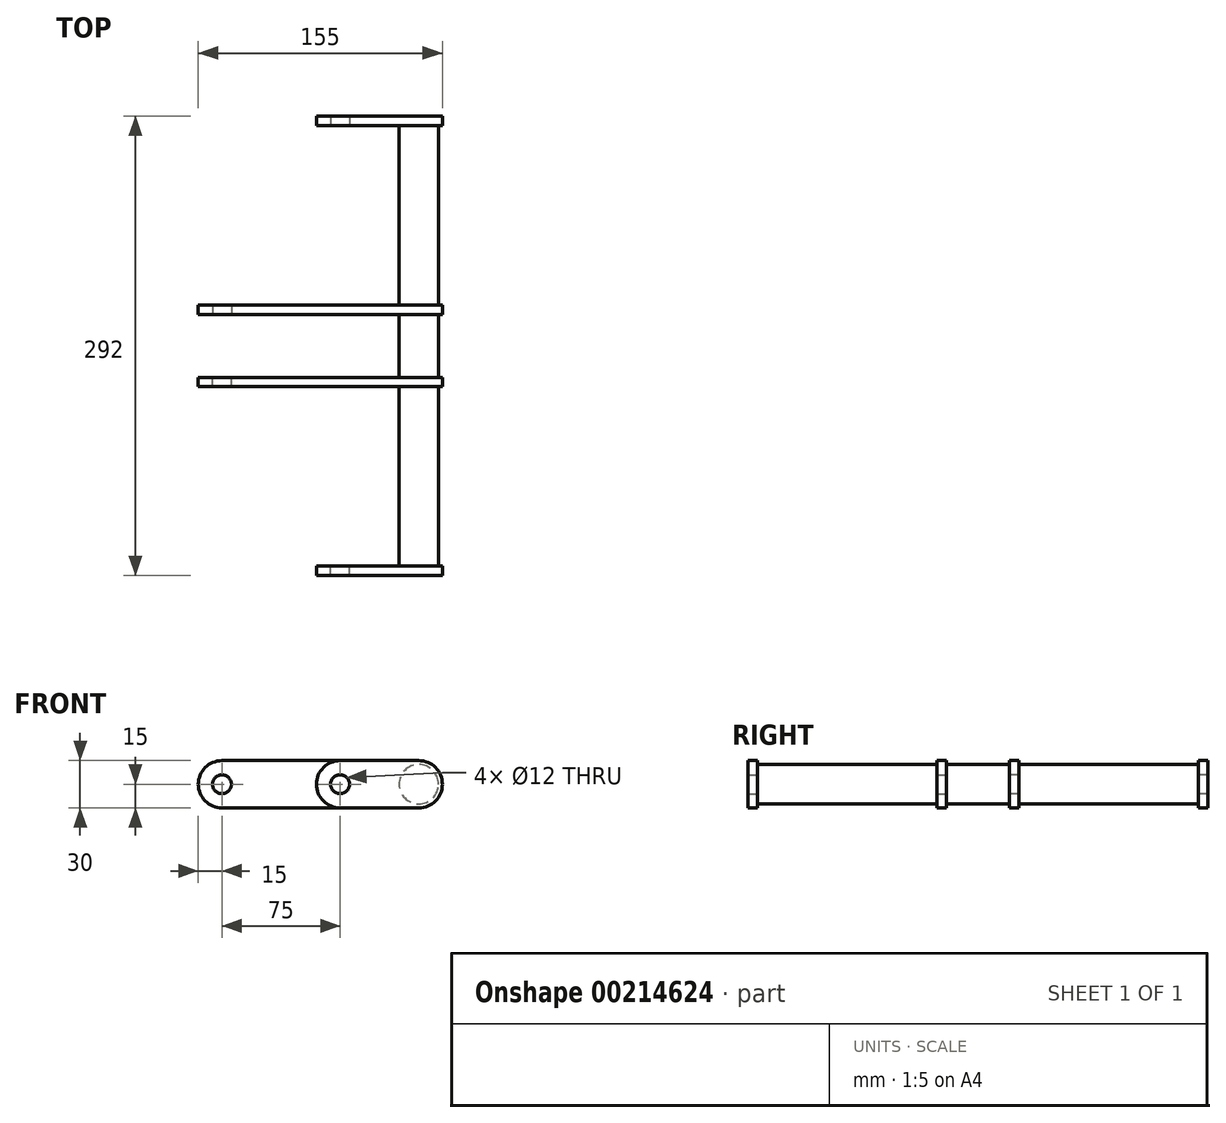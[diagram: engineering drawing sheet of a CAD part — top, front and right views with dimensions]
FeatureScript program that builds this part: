
annotation { "Feature Type Name" : "Feature", "Feature Type Description" : "" }
export const myFeature = defineFeature(function(context is Context, id is Id, definition is map)
    precondition{}
    {
        {
            var Q0;
            Q0=qCreatedBy(makeId("Front.planeOp"),FACE);
            cPlane(context, id + "F0", {"entities" : qUnion([Q0]), "cplaneType" : CPlaneType.OFFSET, "offset" : 140 * mm, "width" : 150 * mm, "height" : 150 * mm});
        }
        {
            var Q0;
            Q0=qCreatedBy(id+"F0.planeOp",FACE);
            var sketch = newSketch(context, id + "F1", { "sketchPlane" : qUnion([Q0])});
            skPoint(sketch, "E0.0", {"position": v(0, 0) * mm});
            skArc(sketch, "E1", {"start": v(0, -15) * mm, "mid": v(15, 0) * mm, "end": v(0, 15) * mm});
            skArc(sketch, "E2", {"start": v(-50, 15) * mm, "mid": v(-65, 0) * mm, "end": v(-50, -15) * mm});
            skCircle(sketch, "E3", {"center": v(0, 0) * mm, "radius": 6 * mm});
            skCircle(sketch, "E4", {"center": v(-50, 0) * mm, "radius": 6 * mm});
            skCircle(sketch, "E5", {"center": v(0, 0) * mm, "radius": 12.5 * mm});
            skLineSegment(sketch, "E6", {"start": v(0, 0) * mm, "end": v(-50, 0) * mm, "construction": true});
            skLineSegment(sketch, "E7", {"start": v(-50, 15) * mm, "end": v(0, 15) * mm});
            skLineSegment(sketch, "E8", {"start": v(0, -15) * mm, "end": v(-50, -15) * mm});
            skSolve(sketch);
        }
        {
            var Q0;
            Q0=makeQuery(id+"F1.imprint","IMPRINT",FACE,{"disambiguationData":[TD([[makeQuery(id+"F1.imprint","IMPRINT",EDGE,{"derivedFrom":sQuery(id+"F1.wireOp",EDGE,"E1")}),1.0]])]});
            var Q1;
            Q1=makeQuery(id+"F1.imprint","IMPRINT",FACE,{"disambiguationData":[TD([[makeQuery(id+"F1.imprint","IMPRINT",EDGE,{"derivedFrom":sQuery(id+"F1.wireOp",EDGE,"E3")}),-1.0]])]});
            var Q2;
            Q2=makeQuery(id+"F1.imprint","IMPRINT",FACE,{"disambiguationData":[TD([[makeQuery(id+"F1.imprint","IMPRINT",EDGE,{"derivedFrom":sQuery(id+"F1.wireOp",EDGE,"E3")}),1.0]])]});
            extrude(context, id + "F2", {"entities" : qUnion([Q0, Q1, Q2]), "depth" : 6 * mm});
        }
        {
            var Q0;
            Q0=makeQuery(id+"F1.imprint","IMPRINT",FACE,{"disambiguationData":[TD([[makeQuery(id+"F1.imprint","IMPRINT",EDGE,{"derivedFrom":sQuery(id+"F1.wireOp",EDGE,"E3")}),-1.0]])]});
            var Q1;
            Q1=makeQuery(id+"F1.imprint","IMPRINT",FACE,{"disambiguationData":[TD([[makeQuery(id+"F1.imprint","IMPRINT",EDGE,{"derivedFrom":sQuery(id+"F1.wireOp",EDGE,"E3")}),1.0]])]});
            var Q2;
            Q2=qCreatedBy(makeId("Front.planeOp"),FACE);
            extrude(context, id + "F3", {"entities" : qUnion([Q0, Q1]), "operationType" : NewBodyOperationType.ADD, "endBound" : BoundingType.UP_TO_SURFACE, "oppositeDirection" : true, "endBoundEntityFace" : qUnion([Q2]), "depth" : 25 * mm});
        }
        {
            var Q0;
            Q0=qCreatedBy(makeId("Front.planeOp"),FACE);
            cPlane(context, id + "F4", {"entities" : qUnion([Q0]), "cplaneType" : CPlaneType.OFFSET, "offset" : 20 * mm, "width" : 150 * mm, "height" : 150 * mm});
        }
        {
            var Q0;
            Q0=qCreatedBy(id+"F4.planeOp",FACE);
            var sketch = newSketch(context, id + "F5", { "sketchPlane" : qUnion([Q0])});
            skArc(sketch, "E9.0", {"start": v(0, -15) * mm, "mid": v(15, 0) * mm, "end": v(0, 15) * mm});
            skArc(sketch, "E10", {"start": v(-125, 15) * mm, "mid": v(-140, 0) * mm, "end": v(-125, -15) * mm});
            skCircle(sketch, "E11", {"center": v(-125, 0) * mm, "radius": 6 * mm});
            skLineSegment(sketch, "E12", {"start": v(-125, 15) * mm, "end": v(0, 15) * mm});
            skLineSegment(sketch, "E13", {"start": v(0, -15) * mm, "end": v(-125, -15) * mm});
            skSolve(sketch);
        }
        {
            var Q0;
            Q0=makeQuery(id+"F5.imprint","IMPRINT",FACE,{"disambiguationData":[TD([[makeQuery(id+"F5.imprint","IMPRINT",EDGE,{"derivedFrom":sQuery(id+"F5.wireOp",EDGE,"E9.0")}),1.0]])]});
            extrude(context, id + "F6", {"entities" : qUnion([Q0]), "operationType" : NewBodyOperationType.ADD, "depth" : 6 * mm});
        }
        {
            var Q0;
            Q0=makeQuery(id+"F2.opExtrude","SWEPT_BODY",BODY,{"disambiguationData":[OSD([sQuery(id+"F1.wireOp",EDGE,"E1"),sQuery(id+"F1.wireOp",EDGE,"E2"),sQuery(id+"F1.wireOp",EDGE,"E4"),sQuery(id+"F1.wireOp",EDGE,"E7"),sQuery(id+"F1.wireOp",EDGE,"E8")])]});
            var Q1;
            Q1=makeQuery(id+"F3.opExtrude","CAP_FACE",FACE,{"disambiguationData":[OSD([sQuery(id+"F1.wireOp",EDGE,"E5")])],"isStart":false});
            mirror(context, id + "F7", {"operationType" : NewBodyOperationType.ADD, "entities" : qUnion([Q0]), "mirrorPlane" : qUnion([Q1])});
        }
    });
